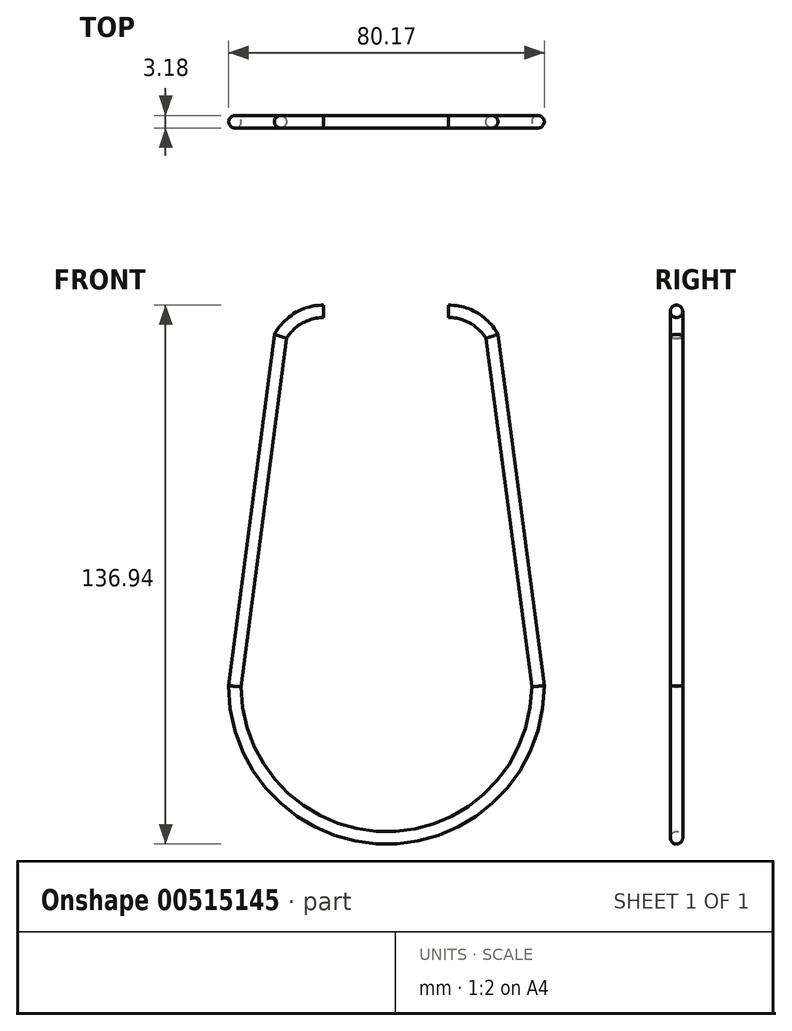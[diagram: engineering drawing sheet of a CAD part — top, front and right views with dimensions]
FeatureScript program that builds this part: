
annotation { "Feature Type Name" : "Feature", "Feature Type Description" : "" }
export const myFeature = defineFeature(function(context is Context, id is Id, definition is map)
    precondition{}
    {
        {
            var Q0;
            Q0=qCreatedBy(makeId("Front.planeOp"),FACE);
            var sketch = newSketch(context, id + "F0", { "sketchPlane" : qUnion([Q0])});
            skArc(sketch, "E0", {"start": v(0, 0) * mm, "mid": v(-6.35, -1.7) * mm, "end": v(-11, -6.35) * mm});
            skArc(sketch, "E1", {"start": v(42.75, -6.35) * mm, "mid": v(38.1, -1.7) * mm, "end": v(31.75, 0) * mm});
            skLineSegment(sketch, "E2", {"start": v(15.88, 0) * mm, "end": v(15.88, -133) * mm, "construction": true});
            skLineSegment(sketch, "E3", {"start": v(-11, -6.35) * mm, "end": v(-22.55, -95.27) * mm});
            skLineSegment(sketch, "E4", {"start": v(42.75, -6.35) * mm, "end": v(54.45, -95.25) * mm});
            skArc(sketch, "E5", {"start": v(-22.55, -95.27) * mm, "mid": v(15.96, -133.76) * mm, "end": v(54.45, -95.25) * mm});
            skSolve(sketch);
        }
        {
            var Q0;
            Q0=qCreatedBy(makeId("Right.planeOp"),FACE);
            var sketch = newSketch(context, id + "F1", { "sketchPlane" : qUnion([Q0])});
            skCircle(sketch, "E6", {"center": v(0, 0) * mm, "radius": 1.59 * mm});
            skSolve(sketch);
        }
        {
            var Q0;
            Q0=makeQuery(id+"F1.imprint","IMPRINT",FACE,{"disambiguationData":[TD([[makeQuery(id+"F1.imprint","IMPRINT",EDGE,{"derivedFrom":sQuery(id+"F1.wireOp",EDGE,"E6")}),1.0]])]});
            var Q1;
            Q1=sQuery(id+"F0.wireOp",EDGE,"E0");
            var Q2;
            Q2=sQuery(id+"F0.wireOp",EDGE,"E3");
            var Q3;
            Q3=sQuery(id+"F0.wireOp",EDGE,"E5");
            var Q4;
            Q4=sQuery(id+"F0.wireOp",EDGE,"E4");
            var Q5;
            Q5=sQuery(id+"F0.wireOp",EDGE,"E1");
            sweep(context, id + "F2", {"profiles" : qUnion([Q0]), "path" : qUnion([Q1, Q2, Q3, Q4, Q5])});
        }
    });
